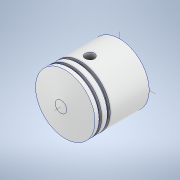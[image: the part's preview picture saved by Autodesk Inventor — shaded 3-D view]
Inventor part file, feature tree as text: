
AUTODESK INVENTOR PART (.ipt)
format: ipt  version: 2021.1 (Build 251245000, 245)  size: 214,016 bytes
history: native  units: in
note: dims shown in document units (in); Inventor stores cm internally (conversion verified against a paired STEP export)
features: projected_geometry x9, sketch x4, extrude x2, revolve x2
ambient origin geometry x8: Origin, YZ Plane, XZ Plane, XY Plane, X Axis, Y Axis, Z Axis, Center Point
bodies: Solid1 (feature_tree)
feature tree (17):
  extrude  "Extrusion1"  Depth=3.2in TaperAngle=0.0deg
  revolve  "Revolution1"  [1 undecoded]
  revolve  "Revolution2"  [1 undecoded]
  extrude  "Extrusion3"  Depth=1.6in
  sketch  "Sketch1"  dims[d0=3.2in d1=3.2in d2=0.0in]
  sketch  "Sketch2"  dims[d3=0.3in d4=2.1in]
  projected_geometry  "Projected Loop1"
  sketch  "Sketch4"  dims[d5=1.45in d6=1.45in]
  projected_geometry  "Projected Loop2"
  sketch  "Sketch5"  dims[d7=0.0687in d8=1.3in d9=1.0in d10=1.0in d11=1.4in d12=90.0deg d17=2.0in d18=90.0deg d19=0.5in d20=1.6in d21=0.0in d22=0.0in]
  projected_geometry  "Projected Loop3"
  projected_geometry  "Projected Loop4"
  projected_geometry  "Projected Loop5"
  projected_geometry  "Project Cut Edges1"
  projected_geometry  "Project Cut Edges2"
  projected_geometry  "Project Cut Edges4"
  projected_geometry  "Project Cut Edges5"
note: 2 required parameter values undecoded (feature->parameter linkage not recoverable at this tier; creation-order binding heuristic only, values carry confidence <= 0.55)
